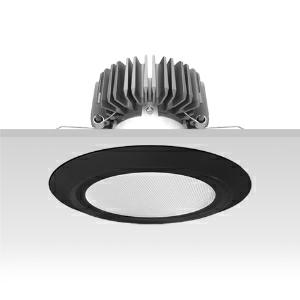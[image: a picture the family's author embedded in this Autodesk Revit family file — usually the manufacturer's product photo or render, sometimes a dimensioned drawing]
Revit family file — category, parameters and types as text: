
# Revit family: 3f_filippi_-_3f_reno_bianco_ampio_3f_filippi_-_30633_a01038_-_3f_reno_200_wh_3000-930_wide___vs_bk_9965
name_source: partatom
category: Lighting Fixtures
units: mm (PartAtom-declared; Revit-internal decimal feet)

## family parameters
Cut with Voids When Loaded = No
Host = Face
Light Source = No
Part Type = Normal
Room Calculation Point = No
Round Connector Dimension = Use Diameter
Shared = No

## types (1)
- 3F Filippi - 3F Reno Bianco Ampio (1 x LED, 2320 lm, 37 W, 3000 K)
    Apparent Load = 37 VA
    Approval mark = CE
    CIE Flux Codes = 75 94 99 100 100
    Color Rendering = 90
    Color Temperature = 3000 K
    Control Gear = Electronic ballast
    Default Elevation = 1800 mm
    Description = ILLUMINOTECHNICAL
Luminous efficiency 100% (DLOR 100%, ULOR 0%).
Initial luminous flux of the luminaire 2320 lm.
Direct symmetric wide distribution.
Installation Interdistance Transv.D = 1.16 x hu - Long.D = 1.14 x hu.
Tabular UGR (CIE 117 - 4H-8H; S=0.25H; 70/50/20): RUG 21.5 - 21.4.
Beam angle: 74° - 74°.
Luminous efficacy 63 lm/W.
Lifetime (L90/B10): 30000 h. (tq+25°C)
Lifetime (L85/B10): 50000 h. (tq+25°C)
Lifetime (L70/B10): 80000 h. (tq+25°C)
Sudden decreased luminous flux after 50000 hours: 0% (C0).
Photobiological safety in compliance with IEC/TR 62778: RG0 risk exempt, (IEC 62471).
In compliance with IEC/EN 62722-2-1 - IEC/EN 62717 standards.

SOURCE
Compact LED module 3000/930.
Energy efficiency class (UE 2019/2020 - UE 2019/2015): E.
CIE 13.3 Colour rendering index: CRI >90 (R9 >50%).
IES TM-30 Fidelity Index: Rf = 92 Rg = 101.
CCT nominal colour temperature 3000 K.
Colour initial tolerance (MacAdam): SDCM 3.
Zhaga Book 3 compliant.

MECHANICAL
Passive heat dissipator in die-casting aluminium, oversized, for optimum thermal management of the LED module.
Parabolic element with graduated/concentric rings in white polycarbonate.
Transparent external lens with glossy and satin differentiated surfaces, with a cooling and anti-insect system in methacrylate (PMMA).
Fastening spring clips in stainless steel.
Dimensions: diameter 226 mm, height 146 mm. Weight 1.775 kg.
IP44 protection degree for exposed part, IP20 for recessed part.
Mechanical strength to impacts IK06 (1 joule).
Glow-wire test resistance 650°C.

ELECTRICAL
Wiring on a separate unit.
Halogen Free electronic wiring 230V-50/60Hz, power factor 0.95, THD <25%, constant output current, SELV, class II, 1 driver.
Power of the luminaire 37 W.
ENEC - CE.
SAFE FLICKER: PstLM=<1 and SVM=<0.4 (IEC TR 61547-1 and IEC TR 63158), to ensure a more comfortable and safe light.
Luminaire compliant with EN 60598-2-22 for power supply from a centralised emergency system CPSS (Central Power Supply System), not incorporated in the luminaire - high risk areas excluded. The default power and flux are 100% in AC and 100% in DC.
Ambient temperature from 0°C to +25°C.
Temperature class T6 max 85°C.
Relative humidity UR: <85%.

INSTALLATION
Pull-up recessed fitting.
False ceiling carving: 200 mm.
All accessories dedicated to this product are available on the Catalog and on our website www.3F-Filippi.com.

ACCESSORIES
A01038 - Anti-glare microprismatic VS moulded glass, tempered, not flammable, locked and in line with the trim, in black polycarbonate.

APPLICATIONS
Environments: architectural, commercial, exhibition areas, transit areas, corridors, shops, display windows, service areas.
In false ceilings with narrow voids.

WARNING
Luminaire designed for disposal/recycling at end-of-life.
Replaceable (LED only) light source by a professional. Replaceable control gear by a professional.
    Height = 0 mm  [stored 0 ft]
    Lamp = 1 x LED
    Lamp Light Flux = 2320 lm
    Lamp Power = 37 W
    Lamp count = 1
    Length = 226 mm
    Lifetime = 50000 h
    Luminous efficacy = 63 lm/W
    Manufacturer = 3F Filippi
    ModVariant = No
    Model = 3F Filippi - 30633+A01038 - 3F Reno 200 WH 3000-930 WIDE + VS BK
    Mounting Place = Ceiling
    Mounting Type = Recessed
    Number of Poles = 1
    OnlyDefault = Yes
    Power Factor = 1
    Product Name = 3F Filippi - 3F Reno Bianco Ampio
    Product group = recessed luminaire
    ProductGroupID = 4
    Protection Class = Protection class II
    Protection Degree = IP 20
    RLX_Detail_Level = 1
    RLX_Emergency_Light_Flux = 0 lm
    RLX_Emergency_Type = 0
    RLX_Emergency_Type_DB = No
    RlxData = <blob elided: 97969 chars, md5=08c04b7f>
    Socket = socket
    Standby Power = 0 W
    System Light Flux = 2320 lm
    System Power = 37 W
    Type Comments = Product without accessories
    Type Image = 3ffilippi_3f_reno_200_bk_vs_smp.jpg
    URL = http://relux.com
    VarID = ---
    Voltage = 0 V
    Weight = 0.00 kg
    Width = 0 mm  [stored 0 ft]

note: [stored X ft] marks values corroborated as IEEE doubles in the binary element streams (Revit-internal decimal feet)

## geometry (parser evidence)
native form markers: Blend x4, Sweep x10
no freeform markers — native parametric forms only
